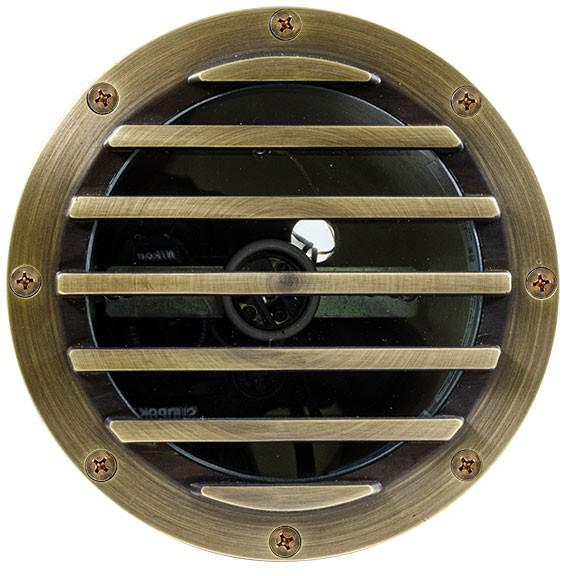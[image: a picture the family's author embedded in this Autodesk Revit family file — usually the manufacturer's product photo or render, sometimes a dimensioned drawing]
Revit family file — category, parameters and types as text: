
# Revit family: Alcon-9034-9-Revit-Family
name_source: partatom
category: Luminarias
units: mm (PartAtom-declared; Revit-internal decimal feet)

## family parameters
Anfitrión = Cara
Compartido = No
Corte con vacíos al cargar = No
Cota de conector redondo = Usar diámetro
Mantener orientación de anotación = No
Origen de luz = Sí
Punto de cálculo de habitación = No
Tipo de pieza = Normal

## types (1)
- Alcon-9034-9-Revit-Family
    Cambio de temperatura de color de luz atenuada = <Ninguno>
    Elevación por defecto = 4' - 0"
    Fabricante = Alcon Lighting
    Filtro de color = 16777215
    GLASS LENS = Analytical Panels
    HOUSING = <Por categoría>
    LENS GLASS = Glass
    Link to IES File = https://www.alconlighting.com
    Longitud de símbolo de origen de luz = 10' - 0"
    Modelo = Alcon Lighting 9034-9
    Product Data URL = https://www.alconlighting.com
    Product Page = https://www.alconlighting.com
    TAP LENS = <Por categoría>
    TOP FINISH = <Por categoría>
    URL = https://www.alconlighting.com
    Ángulo de campo de foco = 90.00°
    Ángulo de enfoque = 30.00°
    Ángulo de inclinación = 60.00°

## geometry (parser evidence)
native form markers: Sweep x3
no freeform markers — native parametric forms only
